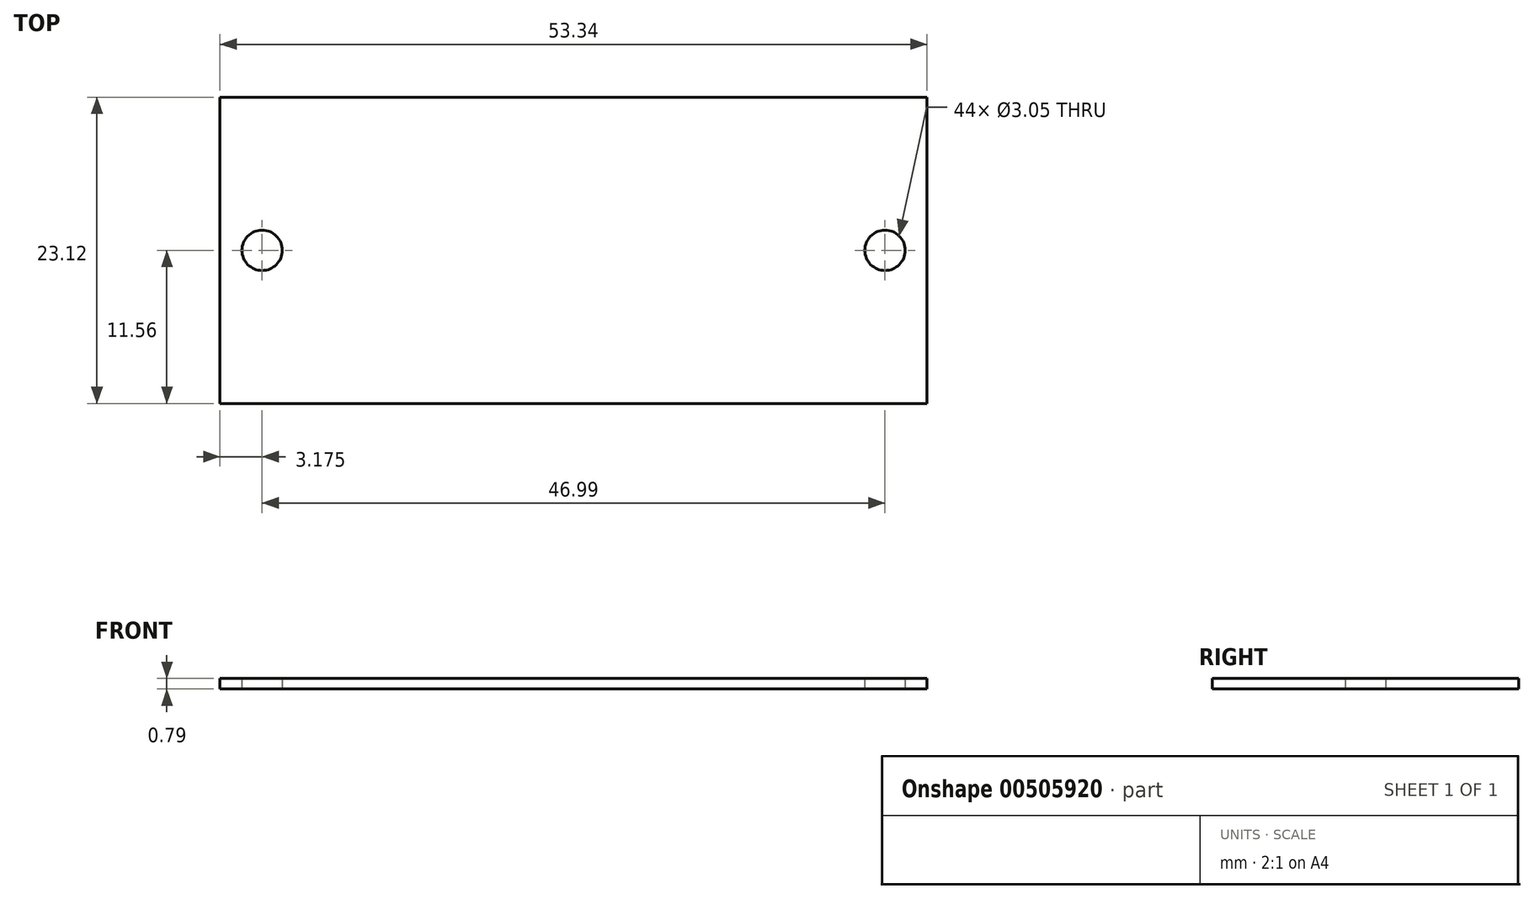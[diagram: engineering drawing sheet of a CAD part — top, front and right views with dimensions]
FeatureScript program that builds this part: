
annotation { "Feature Type Name" : "Feature", "Feature Type Description" : "" }
export const myFeature = defineFeature(function(context is Context, id is Id, definition is map)
    precondition{}
    {
        {
            var Q0;
            Q0=qCreatedBy(makeId("Top.planeOp"),FACE);
            var sketch = newSketch(context, id + "F0", { "sketchPlane" : qUnion([Q0])});
            skLineSegment(sketch, "E0.bottom", {"start": v(20.32, 11.56) * mm, "end": v(-20.32, 11.56) * mm});
            skLineSegment(sketch, "E0.top", {"start": v(20.32, -11.56) * mm, "end": v(-20.32, -11.56) * mm});
            skLineSegment(sketch, "E0.left", {"start": v(20.32, 11.56) * mm, "end": v(20.32, -11.56) * mm});
            skLineSegment(sketch, "E0.right", {"start": v(-20.32, 11.56) * mm, "end": v(-20.32, -11.56) * mm});
            skPoint(sketch, "E0.middle", {"position": v(0, 0) * mm});
            skLineSegment(sketch, "E1.bottom", {"start": v(20.32, 11.56) * mm, "end": v(26.67, 11.56) * mm});
            skLineSegment(sketch, "E1.top", {"start": v(20.32, -11.56) * mm, "end": v(26.67, -11.56) * mm});
            skLineSegment(sketch, "E1.right", {"start": v(26.67, 11.56) * mm, "end": v(26.67, -11.56) * mm});
            skLineSegment(sketch, "E2.bottom", {"start": v(-20.32, 11.56) * mm, "end": v(-26.67, 11.56) * mm});
            skLineSegment(sketch, "E2.top", {"start": v(-20.32, -11.56) * mm, "end": v(-26.67, -11.56) * mm});
            skLineSegment(sketch, "E2.right", {"start": v(-26.67, 11.56) * mm, "end": v(-26.67, -11.56) * mm});
            skLineSegment(sketch, "E3", {"start": v(-26.67, 11.56) * mm, "end": v(-20.32, -11.56) * mm, "construction": true});
            skLineSegment(sketch, "E4", {"start": v(26.67, 11.56) * mm, "end": v(20.32, -11.56) * mm, "construction": true});
            skCircle(sketch, "E5", {"center": v(-23.5, 0) * mm, "radius": 1.52 * mm});
            skCircle(sketch, "E6", {"center": v(23.5, 0) * mm, "radius": 1.52 * mm});
            skLineSegment(sketch, "E7", {"start": v(-23.5, 0) * mm, "end": v(23.5, 0) * mm, "construction": true});
            skSolve(sketch);
        }
        {
            var Q0;
            Q0=makeQuery(id+"F0.imprint","IMPRINT",FACE,{"disambiguationData":[TD([[makeQuery(id+"F0.imprint","IMPRINT",EDGE,{"derivedFrom":sQuery(id+"F0.wireOp",EDGE,"E1.bottom")}),-1.0]])]});
            var Q1;
            Q1=makeQuery(id+"F0.imprint","IMPRINT",FACE,{"disambiguationData":[TD([[makeQuery(id+"F0.imprint","IMPRINT",EDGE,{"derivedFrom":sQuery(id+"F0.wireOp",EDGE,"E0.bottom")}),1.0]])]});
            var Q2;
            Q2=makeQuery(id+"F0.imprint","IMPRINT",FACE,{"disambiguationData":[TD([[makeQuery(id+"F0.imprint","IMPRINT",EDGE,{"derivedFrom":sQuery(id+"F0.wireOp",EDGE,"E2.bottom")}),1.0]])]});
            extrude(context, id + "F1", {"entities" : qUnion([Q0, Q1, Q2]), "depth" : 0.8 * mm});
        }
    });
